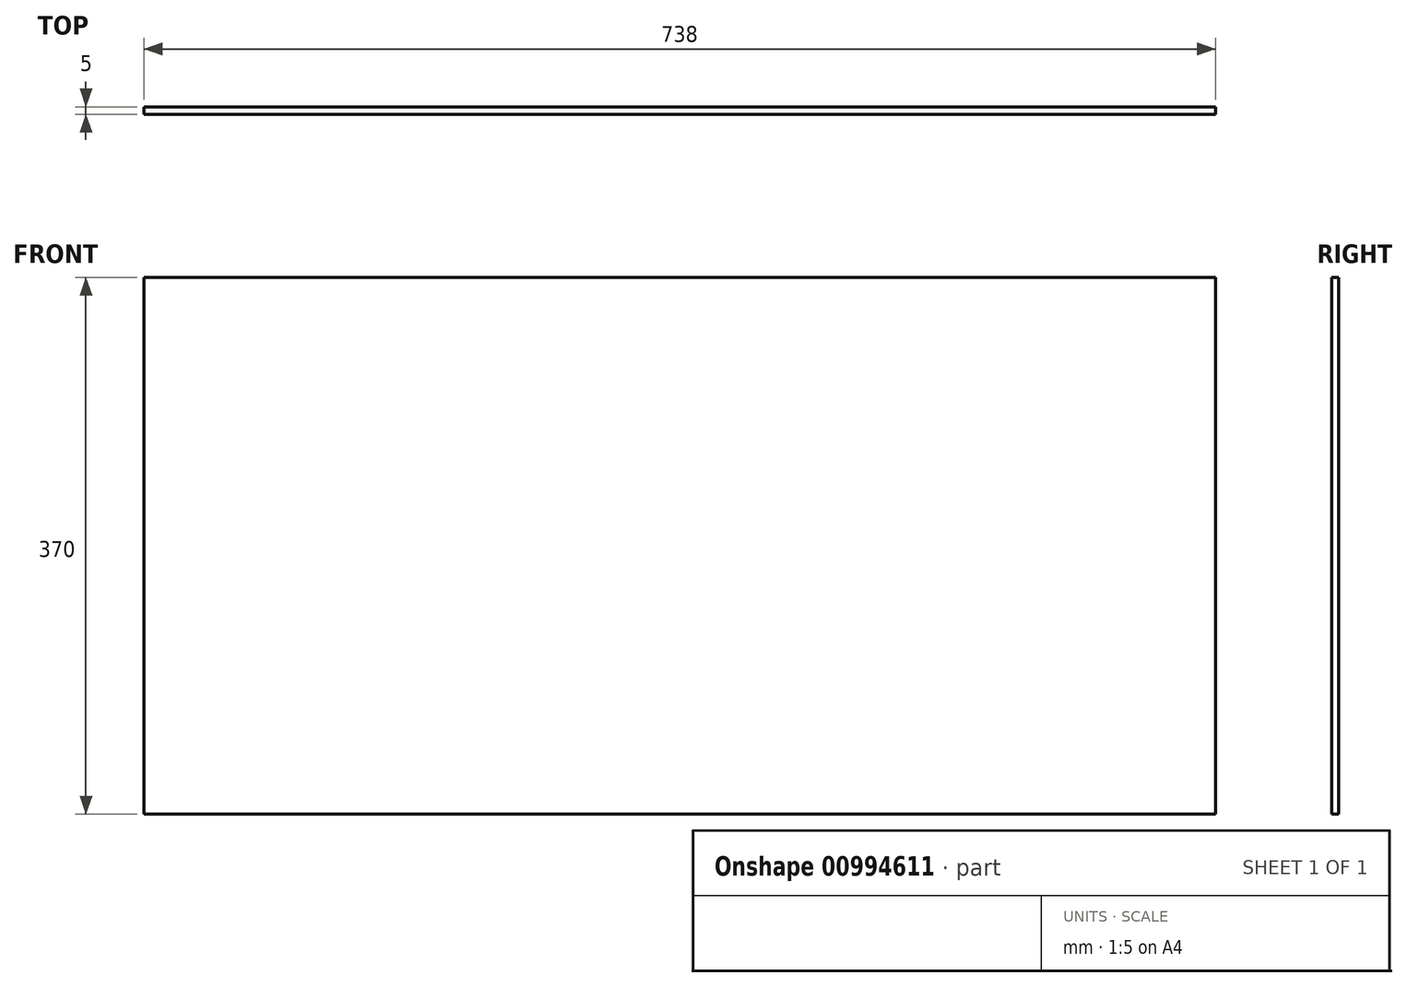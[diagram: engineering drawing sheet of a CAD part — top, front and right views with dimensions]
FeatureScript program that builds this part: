
annotation { "Feature Type Name" : "Feature", "Feature Type Description" : "" }
export const myFeature = defineFeature(function(context is Context, id is Id, definition is map)
    precondition{}
    {
        {
            var Q0;
            Q0=qCreatedBy(makeId("Front.planeOp"),FACE);
            var sketch = newSketch(context, id + "F0", { "sketchPlane" : qUnion([Q0])});
            skLineSegment(sketch, "E0.bottom", {"start": v(-369, -185) * mm, "end": v(369, -185) * mm});
            skLineSegment(sketch, "E0.top", {"start": v(-369, 185) * mm, "end": v(369, 185) * mm});
            skLineSegment(sketch, "E0.left", {"start": v(-369, -185) * mm, "end": v(-369, 185) * mm});
            skLineSegment(sketch, "E0.right", {"start": v(369, -185) * mm, "end": v(369, 185) * mm});
            skPoint(sketch, "E0.middle", {"position": v(0, 0) * mm});
            skSolve(sketch);
        }
        {
            var Q0;
            Q0=makeQuery(id+"F0.imprint","IMPRINT",FACE,{"disambiguationData":[TD([[makeQuery(id+"F0.imprint","IMPRINT",EDGE,{"derivedFrom":sQuery(id+"F0.wireOp",EDGE,"E0.bottom")}),1.0]])]});
            extrude(context, id + "F1", {"entities" : qUnion([Q0]), "depth" : 5 * mm, "offsetDistance" : 25 * mm});
        }
    });
